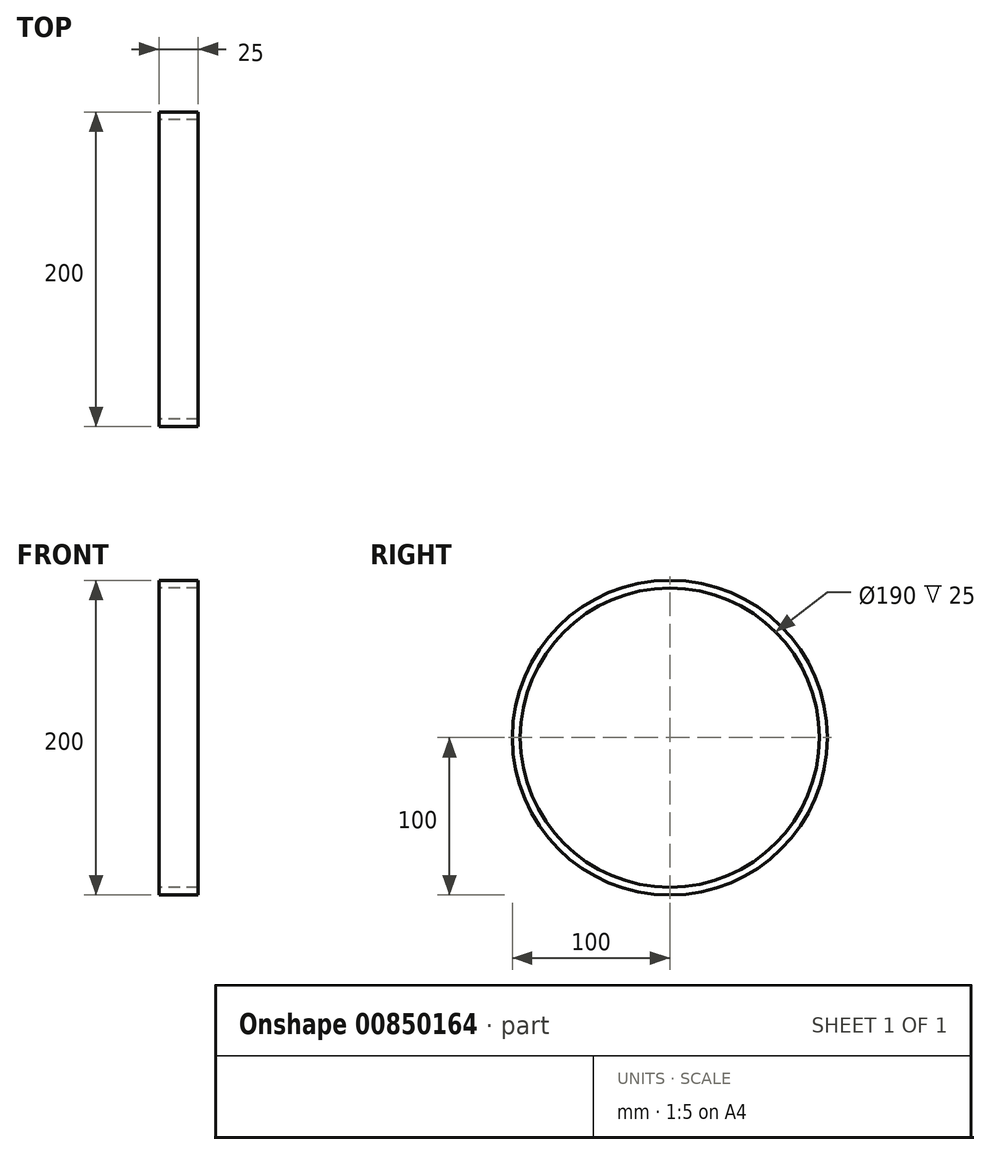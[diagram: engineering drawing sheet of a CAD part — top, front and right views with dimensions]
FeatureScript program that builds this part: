
annotation { "Feature Type Name" : "Feature", "Feature Type Description" : "" }
export const myFeature = defineFeature(function(context is Context, id is Id, definition is map)
    precondition{}
    {
        {
            var Q0;
            Q0=qCreatedBy(makeId("Right.planeOp"),FACE);
            var sketch = newSketch(context, id + "F0", { "sketchPlane" : qUnion([Q0])});
            skCircle(sketch, "E0", {"center": v(0, 0) * mm, "radius": 100 * mm});
            skCircle(sketch, "E1", {"center": v(0, 0) * mm, "radius": 95 * mm});
            skSolve(sketch);
        }
        {
            var Q0;
            Q0=makeQuery(id+"F0.imprint","IMPRINT",FACE,{"disambiguationData":[TD([[makeQuery(id+"F0.imprint","IMPRINT",EDGE,{"derivedFrom":sQuery(id+"F0.wireOp",EDGE,"E0")}),1.0]])]});
            extrude(context, id + "F1", {"entities" : qUnion([Q0]), "depth" : 25 * mm});
        }
        {
            var Q0;
            Q0=qCreatedBy(makeId("Front.planeOp"),FACE);
            cPlane(context, id + "F2", {"entities" : qUnion([Q0]), "cplaneType" : CPlaneType.OFFSET, "offset" : 100 * mm, "width" : 150 * mm, "height" : 150 * mm});
        }
    });
